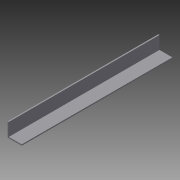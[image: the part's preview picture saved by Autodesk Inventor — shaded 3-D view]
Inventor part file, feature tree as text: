
AUTODESK INVENTOR PART (.ipt)
format: ipt  version: 2015 (Build 190159000, 159)  size: 88,576 bytes
history: native  units: in
note: dims shown in document units (in); Inventor stores cm internally (conversion verified against a paired STEP export)
features: extrude x3, sketch x3
ambient origin geometry x8: Origin, YZ Plane, XZ Plane, XY Plane, X Axis, Y Axis, Z Axis, Center Point
bodies: Solid1 (feature_tree)
feature tree (6):
  extrude  "Extrusion1"  Depth=0.125in
  extrude  "Extrusion2"  Depth=0.125in
  extrude  "Extrusion3"  Depth=1.5in TaperAngle=0.0deg
  sketch  "Sketch1"  dims[d0=1.5in d1=0.125in]
  sketch  "Sketch2"  dims[d2=14.0in d3=0.0in d4=0.125in]
  sketch  "Sketch3"  dims[d5=1.5in d6=14.0in d7=0.0in d8=2.0in d9=0.0in]
